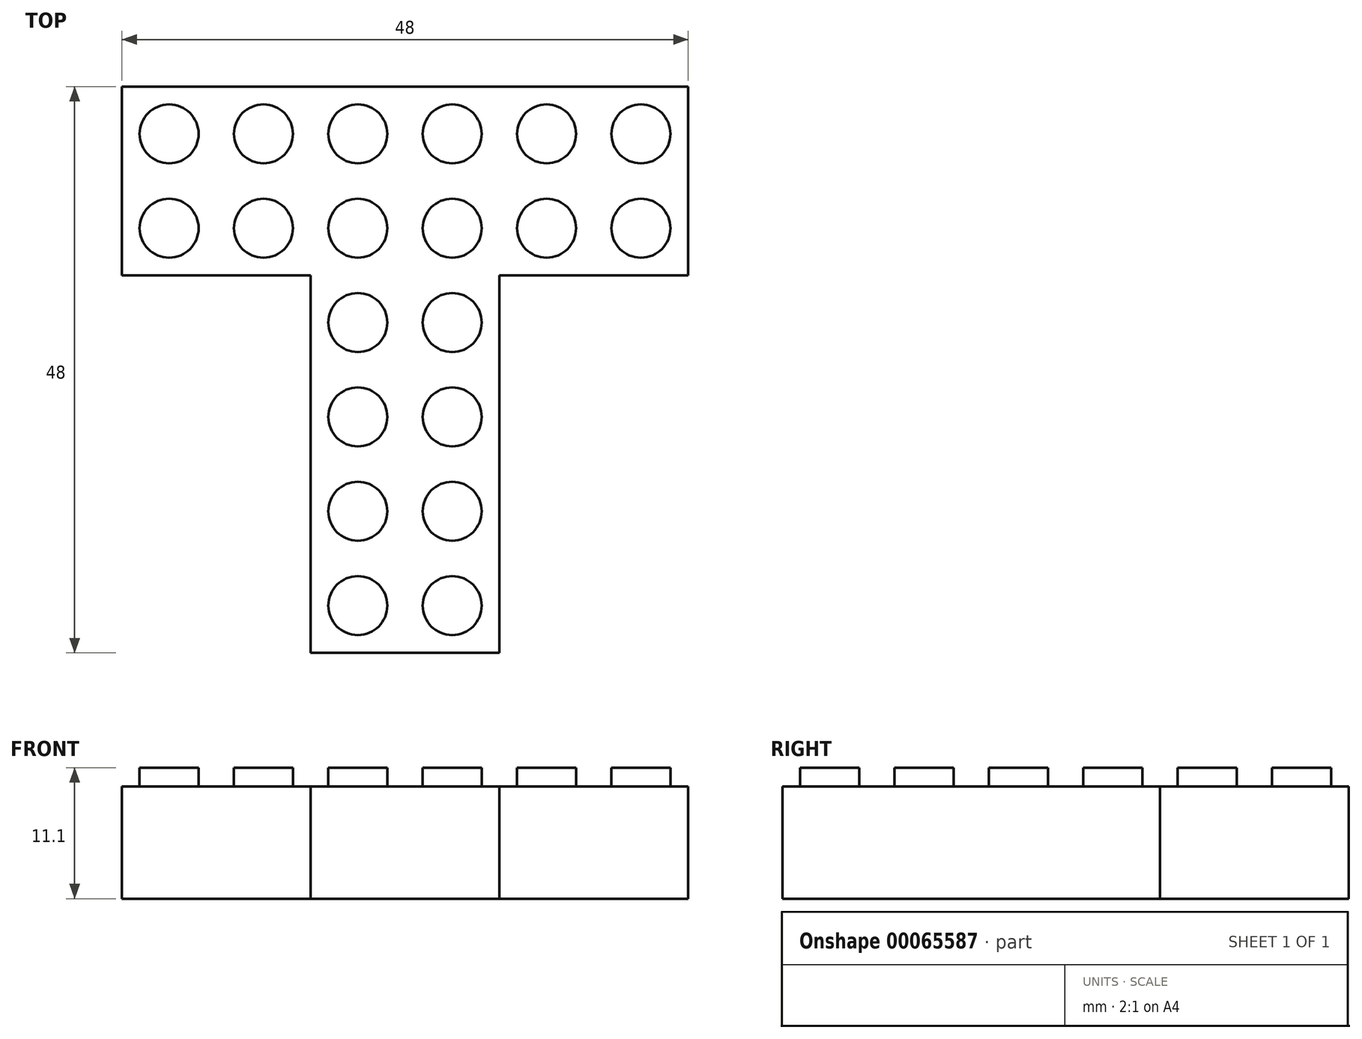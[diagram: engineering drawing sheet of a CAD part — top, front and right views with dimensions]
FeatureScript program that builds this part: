
annotation { "Feature Type Name" : "Feature", "Feature Type Description" : "" }
export const myFeature = defineFeature(function(context is Context, id is Id, definition is map)
    precondition{}
    {
        {
            var Q0;
            Q0=qCreatedBy(makeId("Top.planeOp"),FACE);
            var sketch = newSketch(context, id + "F0", { "sketchPlane" : qUnion([Q0])});
            skLineSegment(sketch, "E0.rect.bottom", {"start": v(8, -24) * mm, "end": v(-8, -24) * mm});
            skLineSegment(sketch, "E0.rect.top", {"start": v(8, 24) * mm, "end": v(-8, 24) * mm});
            skLineSegment(sketch, "E0.rect.left", {"start": v(8, -24) * mm, "end": v(8, 24) * mm});
            skLineSegment(sketch, "E0.rect.right", {"start": v(-8, -24) * mm, "end": v(-8, 24) * mm});
            skPoint(sketch, "E0.rect.middle", {"position": v(0, 0) * mm});
            skLineSegment(sketch, "E1.bottom", {"start": v(8, 24) * mm, "end": v(24, 24) * mm});
            skLineSegment(sketch, "E1.top", {"start": v(8, 8) * mm, "end": v(24, 8) * mm});
            skLineSegment(sketch, "E1.left", {"start": v(8, 24) * mm, "end": v(8, 8) * mm});
            skLineSegment(sketch, "E1.right", {"start": v(24, 24) * mm, "end": v(24, 8) * mm});
            skLineSegment(sketch, "E2.bottom", {"start": v(-8, 24) * mm, "end": v(-24, 24) * mm});
            skLineSegment(sketch, "E2.top", {"start": v(-8, 8) * mm, "end": v(-24, 8) * mm});
            skLineSegment(sketch, "E2.left", {"start": v(-8, 24) * mm, "end": v(-8, 8) * mm});
            skLineSegment(sketch, "E2.right", {"start": v(-24, 24) * mm, "end": v(-24, 8) * mm});
            skSolve(sketch);
        }
        {
            var Q0;
            Q0 = qSketchRegion(id + "F0", true);
            extrude(context, id + "F1", {"entities" : qUnion([Q0]), "depth" : 9.5 * mm});
        }
        {
            var Q0;
            Q0=makeQuery(id+"F1.opExtrude","CAP_FACE",FACE,{"disambiguationData":[OSD([sQuery(id+"F0.wireOp",EDGE,"E0.rect.bottom"),sQuery(id+"F0.wireOp",EDGE,"E0.rect.top"),sQuery(id+"F0.wireOp",EDGE,"E0.rect.left"),sQuery(id+"F0.wireOp",EDGE,"E0.rect.right"),sQuery(id+"F0.wireOp",EDGE,"E1.bottom"),sQuery(id+"F0.wireOp",EDGE,"E1.top"),sQuery(id+"F0.wireOp",EDGE,"E1.right"),sQuery(id+"F0.wireOp",EDGE,"E2.bottom"),sQuery(id+"F0.wireOp",EDGE,"E2.top"),sQuery(id+"F0.wireOp",EDGE,"E2.right")])],"isStart":false});
            var sketch = newSketch(context, id + "F2", { "sketchPlane" : qUnion([Q0])});
            skPoint(sketch, "E3.rect.middle", {"position": v(-16, 16) * mm});
            skPoint(sketch, "E4.rect.middle", {"position": v(0, 16) * mm});
            skPoint(sketch, "E5.rect.middle", {"position": v(16, 16) * mm});
            skPoint(sketch, "E6.rect.middle", {"position": v(0, 0) * mm});
            skPoint(sketch, "E7.rect.middle", {"position": v(0, -16) * mm});
            skCircle(sketch, "E8", {"center": v(-20, 20) * mm, "radius": 2.5 * mm});
            skCircle(sketch, "E9", {"center": v(-20, 12) * mm, "radius": 2.5 * mm});
            skCircle(sketch, "E10.MirrorC", {"center": v(-12, 20) * mm, "radius": 2.5 * mm});
            skCircle(sketch, "E11.MirrorC", {"center": v(-12, 12) * mm, "radius": 2.5 * mm});
            skCircle(sketch, "E12.MirrorC", {"center": v(-4, 20) * mm, "radius": 2.5 * mm});
            skCircle(sketch, "E13.MirrorC", {"center": v(-4, 12) * mm, "radius": 2.5 * mm});
            skCircle(sketch, "E14.MirrorC", {"center": v(4, 20) * mm, "radius": 2.5 * mm});
            skCircle(sketch, "E15.MirrorC", {"center": v(4, 12) * mm, "radius": 2.5 * mm});
            skCircle(sketch, "E16.MirrorC", {"center": v(12, 12) * mm, "radius": 2.5 * mm});
            skCircle(sketch, "E17.MirrorC", {"center": v(12, 20) * mm, "radius": 2.5 * mm});
            skCircle(sketch, "E18.MirrorC", {"center": v(20, 20) * mm, "radius": 2.5 * mm});
            skCircle(sketch, "E19.MirrorC", {"center": v(20, 12) * mm, "radius": 2.5 * mm});
            skCircle(sketch, "E20.MirrorC", {"center": v(-4, 4) * mm, "radius": 2.5 * mm});
            skCircle(sketch, "E21.MirrorC", {"center": v(4, 4) * mm, "radius": 2.5 * mm});
            skCircle(sketch, "E22.MirrorC", {"center": v(-4, -4) * mm, "radius": 2.5 * mm});
            skCircle(sketch, "E23.MirrorC", {"center": v(4, -4) * mm, "radius": 2.5 * mm});
            skCircle(sketch, "E24.MirrorC", {"center": v(4, -12) * mm, "radius": 2.5 * mm});
            skCircle(sketch, "E25.MirrorC", {"center": v(-4, -12) * mm, "radius": 2.5 * mm});
            skCircle(sketch, "E26.MirrorC", {"center": v(-4, -20) * mm, "radius": 2.5 * mm});
            skCircle(sketch, "E27.MirrorC", {"center": v(4, -20) * mm, "radius": 2.5 * mm});
            skSolve(sketch);
        }
        {
            var Q0;
            Q0 = qSketchRegion(id + "F2", true);
            extrude(context, id + "F3", {"entities" : qUnion([Q0]), "operationType" : NewBodyOperationType.ADD, "depth" : 1.6 * mm});
        }
    });
